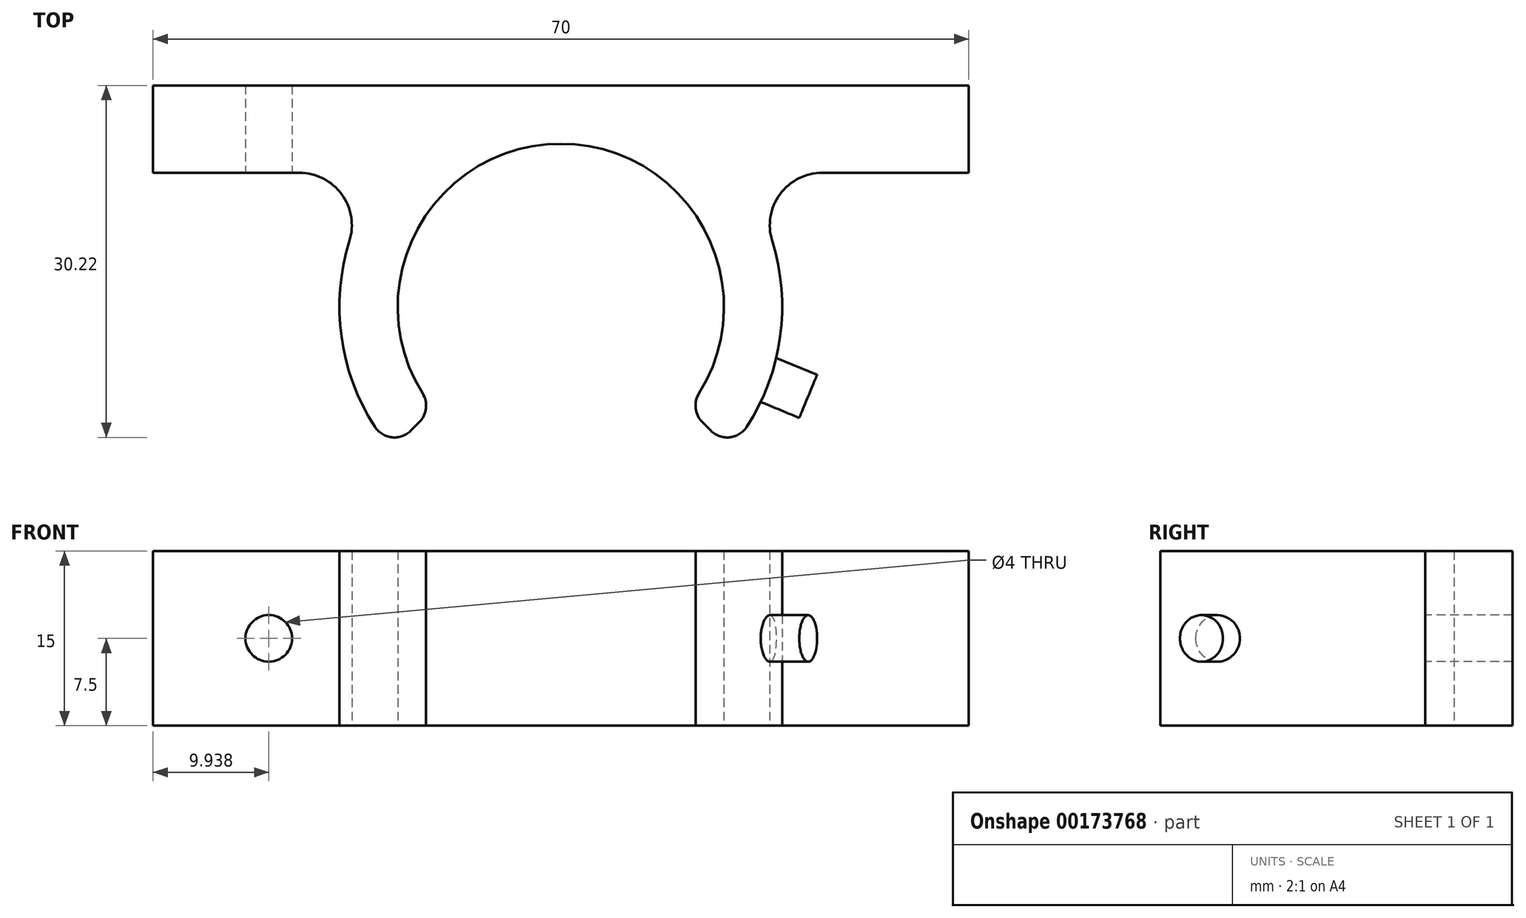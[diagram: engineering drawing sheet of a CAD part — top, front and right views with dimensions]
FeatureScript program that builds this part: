
annotation { "Feature Type Name" : "Feature", "Feature Type Description" : "" }
export const myFeature = defineFeature(function(context is Context, id is Id, definition is map)
    precondition{}
    {
        {
            var Q0;
            Q0=qCreatedBy(makeId("Right.planeOp"),FACE);
            var sketch = newSketch(context, id + "F0", { "sketchPlane" : qUnion([Q0])});
            skCircle(sketch, "E0", {"center": v(0, 0) * mm, "radius": 14 * mm});
            skLineSegment(sketch, "E1", {"start": v(0, 0) * mm, "end": v(-14, 0) * mm, "construction": true});
            skLineSegment(sketch, "E2", {"start": v(0, 0) * mm, "end": v(-8.72, 10.96) * mm, "construction": true});
            skLineSegment(sketch, "E3.MirrorCS", {"start": v(0, 0) * mm, "end": v(-8.72, -10.96) * mm, "construction": true});
            skCircle(sketch, "E4.0", {"center": v(0, 0) * mm, "radius": 19 * mm});
            skLineSegment(sketch, "E5", {"start": v(-8.72, 10.96) * mm, "end": v(-12.27, 14.5) * mm});
            skLineSegment(sketch, "E6", {"start": v(-8.72, 10.96) * mm, "end": v(-14.61, 10.96) * mm, "construction": true});
            skLineSegment(sketch, "E7.MirrorCS", {"start": v(-8.72, -10.96) * mm, "end": v(-12.27, -14.5) * mm});
            skPoint(sketch, "E8", {"position": v(19, 0) * mm});
            skLineSegment(sketch, "E9", {"start": v(19, 35) * mm, "end": v(19, -35) * mm});
            skLineSegment(sketch, "E10", {"start": v(19, 35) * mm, "end": v(11.5, 35) * mm});
            skLineSegment(sketch, "E11", {"start": v(11.5, 35) * mm, "end": v(11.5, 15.12) * mm});
            skLineSegment(sketch, "E12.MirrorCS", {"start": v(11.5, -35) * mm, "end": v(11.5, -15.12) * mm});
            skLineSegment(sketch, "E13.MirrorCS", {"start": v(19, -35) * mm, "end": v(11.5, -35) * mm});
            skSolve(sketch);
        }
        {
            var Q0;
            {var subQ3=sQuery(id+"F0.wireOp",EDGE,"E5");Q0=makeQuery(id+"F0.imprint","IMPRINT",FACE,{"disambiguationData":[TD([[makeQuery(id+"F0.imprint","IMPRINT",EDGE,{"derivedFrom":subQ3}),-1.0]])]});}
            var Q1;
            {var subQ4=sQuery(id+"F0.wireOp",EDGE,"E10");Q1=makeQuery(id+"F0.imprint","IMPRINT",FACE,{"disambiguationData":[TD([[makeQuery(id+"F0.imprint","IMPRINT",EDGE,{"derivedFrom":subQ4}),1.0]])]});}
            var Q2;
            {var subQ0=sQuery(id+"F0.wireOp",EDGE,"E12.MirrorCS");Q2=makeQuery(id+"F0.imprint","IMPRINT",FACE,{"disambiguationData":[TD([[makeQuery(id+"F0.imprint","IMPRINT",EDGE,{"derivedFrom":subQ0}),-1.0]])]});}
            extrude(context, id + "F1", {"entities" : qUnion([Q0, Q1, Q2]), "depth" : 15 * mm});
        }
        {
            var Q0;
            Q0=makeQuery(id+"F1.opExtrude","SWEPT_FACE",FACE,{"disambiguationData":[OSD([sQuery(id+"F0.wireOp",EDGE,"E11")])]});
            var sketch = newSketch(context, id + "F2", { "sketchPlane" : qUnion([Q0])});
            skLineSegment(sketch, "E14", {"start": v(7.5, 35) * mm, "end": v(7.5, -35) * mm, "construction": true});
            skLineSegment(sketch, "E15", {"start": v(15, 25.06) * mm, "end": v(0, 25.06) * mm, "construction": true});
            skLineSegment(sketch, "E16", {"start": v(0, 0) * mm, "end": v(14.94, 0) * mm, "construction": true});
            skCircle(sketch, "E17", {"center": v(7.5, 25.06) * mm, "radius": 2 * mm});
            skCircle(sketch, "E18.MirrorC", {"center": v(7.5, -25.06) * mm, "radius": 2 * mm});
            skSolve(sketch);
        }
        {
            var Q0;
            Q0=makeQuery(id+"F2.imprint","IMPRINT",FACE,{"disambiguationData":[TD([[makeQuery(id+"F2.imprint","IMPRINT",EDGE,{"derivedFrom":sQuery(id+"F2.wireOp",EDGE,"E17")}),1.0]])]});
            var Q1;
            Q1=makeQuery(id+"F2.imprint","IMPRINT",FACE,{"disambiguationData":[TD([[makeQuery(id+"F2.imprint","IMPRINT",EDGE,{"derivedFrom":sQuery(id+"F2.wireOp",EDGE,"E18.MirrorC")}),-1.0]])]});
            var Q2;
            Q2=makeQuery(id+"F1.opExtrude","SWEPT_FACE",FACE,{"disambiguationData":[OSD([sQuery(id+"F0.wireOp",EDGE,"E9")])]});
            extrude(context, id + "F3", {"entities" : qUnion([Q0, Q1]), "operationType" : NewBodyOperationType.REMOVE, "endBound" : BoundingType.UP_TO_SURFACE, "oppositeDirection" : true, "endBoundEntityFace" : qUnion([Q2]), "depth" : 25 * mm});
        }
        {
            var Q0;
            Q0=makeQuery(id+"F1.opExtrude","SWEPT_BODY",BODY,{"disambiguationData":[OSD([sQuery(id+"F0.wireOp",EDGE,"E0"),sQuery(id+"F0.wireOp",EDGE,"E4.0"),sQuery(id+"F0.wireOp",EDGE,"E5"),sQuery(id+"F0.wireOp",EDGE,"E7.MirrorCS"),sQuery(id+"F0.wireOp",EDGE,"E9"),sQuery(id+"F0.wireOp",EDGE,"E10"),sQuery(id+"F0.wireOp",EDGE,"E11"),sQuery(id+"F0.wireOp",EDGE,"E12.MirrorCS"),sQuery(id+"F0.wireOp",EDGE,"E13.MirrorCS")])]});
            var Q1;
            Q1=sQuery(id+"F2.wireOp",EDGE,"E16");
            var Q2;
            Q2=sQuery(id+"F0.wireOp",EDGE,"E1");
            transform(context, id + "F4", {"entities" : qUnion([Q0]), "transformType" : TransformType.ROTATION, "transformAxis" : qUnion([Q2]), "angle" : 90 * degree, "makeCopy" : false});
        }
        {
            var Q0;
            Q0=makeQuery(id+"F1.opExtrude","SWEPT_EDGE",EDGE,{"disambiguationData":[OSD([sQuery(id+"F0.wireOp",EDGE,"E4.0"),sQuery(id+"F0.wireOp",EDGE,"E11")])]});
            var Q1;
            Q1=makeQuery(id+"F1.opExtrude","SWEPT_EDGE",EDGE,{"disambiguationData":[OSD([sQuery(id+"F0.wireOp",EDGE,"E4.0"),sQuery(id+"F0.wireOp",EDGE,"E12.MirrorCS")])]});
            fillet(context, id + "F5", {"entities" : qUnion([Q0, Q1]), "radius" : 4.5 * mm, "tangentPropagation" : true, "allowEdgeOverflow" : false});
        }
        {
            var Q0;
            Q0=makeQuery(id+"F1.opExtrude","SWEPT_EDGE",EDGE,{"disambiguationData":[OSD([sQuery(id+"F0.wireOp",EDGE,"E0"),sQuery(id+"F0.wireOp",EDGE,"E7.MirrorCS")])]});
            var Q1;
            Q1=makeQuery(id+"F1.opExtrude","SWEPT_EDGE",EDGE,{"disambiguationData":[OSD([sQuery(id+"F0.wireOp",EDGE,"E0"),sQuery(id+"F0.wireOp",EDGE,"E5")])]});
            var Q2;
            Q2=makeQuery(id+"F1.opExtrude","SWEPT_EDGE",EDGE,{"disambiguationData":[OSD([sQuery(id+"F0.wireOp",EDGE,"E4.0"),sQuery(id+"F0.wireOp",EDGE,"E5")])]});
            var Q3;
            Q3=makeQuery(id+"F1.opExtrude","SWEPT_EDGE",EDGE,{"disambiguationData":[OSD([sQuery(id+"F0.wireOp",EDGE,"E4.0"),sQuery(id+"F0.wireOp",EDGE,"E7.MirrorCS")])]});
            fillet(context, id + "F6", {"entities" : qUnion([Q0, Q1, Q2, Q3]), "radius" : 2 * mm, "tangentPropagation" : true, "allowEdgeOverflow" : false});
        }
        {
            var Q0;
            Q0=qCreatedBy(makeId("Right.planeOp"),FACE);
            var Q1;
            Q1=sQuery(id+"F0.wireOp",EDGE,"E9");
            cPlane(context, id + "F7", {"entities" : qUnion([Q0, Q1]), "cplaneType" : CPlaneType.LINE_ANGLE, "offset" : 25 * mm, "angle" : 315 * degree, "width" : 150 * mm, "height" : 150 * mm});
        }
        {
            var Q0;
            Q0=qCreatedBy(id+"F7.planeOp",FACE);
            var sketch = newSketch(context, id + "F8", { "sketchPlane" : qUnion([Q0])});
            skLineSegment(sketch, "E19", {"start": v(13.44, 15) * mm, "end": v(13.44, 0) * mm});
            skSolve(sketch);
        }
        {
            var Q0;
            Q0=sQuery(id+"F8.wireOp",EDGE,"E19");
            cPlane(context, id + "F9", {"entities" : qUnion([Q0]), "cplaneType" : CPlaneType.LINE_ANGLE, "offset" : 25 * mm, "angle" : 22.5 * degree, "width" : 150 * mm, "height" : 150 * mm});
        }
        {
            var Q0;
            Q0=qCreatedBy(id+"F9.planeOp",FACE);
            var sketch = newSketch(context, id + "F10", { "sketchPlane" : qUnion([Q0])});
            skLineSegment(sketch, "E20", {"start": v(-7.12, 7.5) * mm, "end": v(5.08, 7.5) * mm, "construction": true});
            skCircle(sketch, "E21", {"center": v(-1.02, 7.5) * mm, "radius": 2 * mm});
            skSolve(sketch);
        }
        {
            var Q0;
            Q0=qSketchRegion(id+"F10",true);
            extrude(context, id + "F11", {"entities" : qUnion([Q0]), "operationType" : NewBodyOperationType.ADD, "oppositeDirection" : true, "depth" : 5 * mm});
        }
    });
